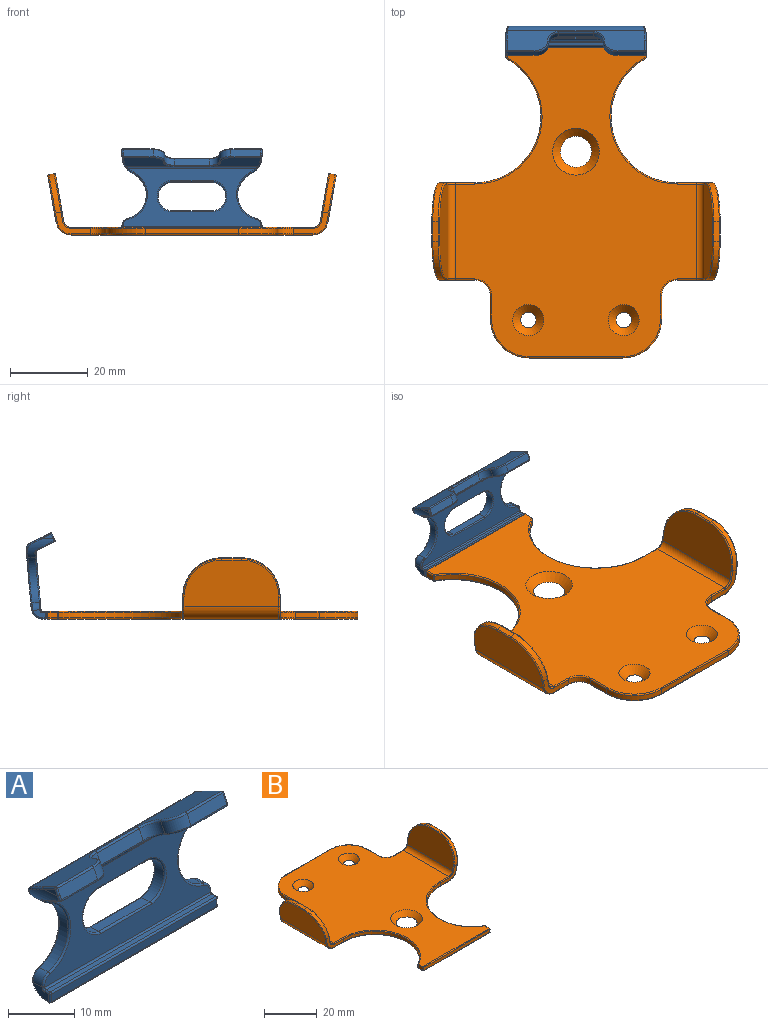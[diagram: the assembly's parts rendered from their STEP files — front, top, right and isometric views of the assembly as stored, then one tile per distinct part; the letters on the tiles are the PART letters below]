
ASSEMBLY  parts=2 mates=1
PART A: 107 faces, bbox 36.3x7.8x22.5 mm
  f0: plane 35.4x14.87mm, normal (0,-1,0.09), area 267.4mm2, adj f16,f17,f25,f26,f27,f28,f43,f44
  f1: plane 35.22x14.86mm, normal (0,1,-0.09), area 265.9mm2, adj f10,f15,f29,f30,f31,f32,f52,f53
  f2: plane 3.27x2.09mm, normal (1,0,0), area 4.5mm2, adj f35,f56,f57,f72,f73,f74,f102
  f3: plane 3.27x2.09mm, normal (-1,0,0), area 4.5mm2, adj f36,f46,f47,f48,f58,f59,f103
  f4: plane 11.89x4.49mm, normal (0,-0.45,-0.89), area 50.1mm2, adj f16,f41,f85,f87,f89
  f5: plane 35.4x5.1mm, normal (0,0.45,0.89), area 124.1mm2, adj f10,f49,f50,f65,f66,f86,f88,f90
  f6: plane 7.7x1.7mm, normal (0,-0.89,0.45), area 14.6mm2, adj f39,f76,f80,f82,f86
  f7: plane 35.4x0.82mm, normal (0,0,1), area 29.1mm2, adj f17,f48,f74,f106
  f8: plane 35.4x1.4mm, normal (0,-1,0), area 49.6mm2, adj f99,f102,f103,f106
  f9: plane 35.4x0.68mm, normal (0,0,-1), area 24.2mm2, adj f15,f57,f58,f99
  f10: cylinder r=2mm len=35.17mm, axis (-1,0,0), area 82.8mm2, adj f1,f5,f51,f64
  f11: plane 7.7x1.7mm, normal (0,-0.89,0.45), area 14.6mm2, adj f40,f89,f93,f95,f98
  f12: plane 11.89x4.49mm, normal (0,-0.45,-0.89), area 50.1mm2, adj f16,f67,f75,f76,f77
  f13: plane 3.08x1.29mm, normal (1,0,0), area 1.6mm2, adj f33,f49,f82
  f14: plane 3.08x1.29mm, normal (-1,0,0), area 1.6mm2, adj f34,f66,f95
  f15: cylinder r=3mm len=35.4mm, axis (-1,0,0), area 157.5mm2, adj f1,f9,f55,f56,f59,f60
  f16: cylinder r=0.5mm len=33.89mm, axis (1,0,0), area 17.9mm2, adj f0,f4,f12,f42,f68,f79,f81,f83
  f17: cylinder r=0.3mm len=35.4mm, axis (1,0,0), area 15.8mm2, adj f0,f7,f47,f73
  f18: plane 9x1.75mm, normal (0,-0.89,0.45), area 17.6mm2, adj f37,f38,f81,f92
  f19: cylinder r=6.25mm len=11.78mm, axis (0,1,-0.09), area 28.9mm2, adj f34,f36,f44,f62
  f20: cylinder r=6.25mm len=11.78mm, axis (0,1,-0.09), area 28.9mm2, adj f33,f35,f53,f70
  f21: plane 11x1.89mm, normal (0,0.09,1), area 20.9mm2, adj f22,f24,f26,f29
  f22: cylinder r=3.8mm len=7.64mm, axis (0,1,-0.09), area 20.3mm2, adj f21,f23,f25,f30
  f23: plane 11x1.89mm, normal (0,-0.09,-1), area 20.9mm2, adj f22,f24,f27,f32
  f24: cylinder r=3.8mm len=7.64mm, axis (0,1,-0.09), area 20.3mm2, adj f21,f23,f28,f31
  f25: torus R=4.1mm, axis (0,1,-0.09), area 5.2mm2, adj f0,f22,f26,f27
  f26: cylinder r=0.3mm len=11.05mm, axis (1,0,0), area 5.2mm2, adj f0,f21,f25,f28
  f27: cylinder r=0.3mm len=11.05mm, axis (-1,0,0), area 5.2mm2, adj f0,f23,f25,f28
  f28: torus R=4.1mm, axis (0,1,-0.09), area 5.2mm2, adj f0,f24,f26,f27
  f29: cylinder r=0.3mm len=11.05mm, axis (-1,0,0), area 5.2mm2, adj f1,f21,f30,f31
  f30: torus R=4.1mm, axis (0,-1,0.09), area 5.2mm2, adj f1,f22,f29,f32
  f31: torus R=4.1mm, axis (0,-1,0.09), area 5.2mm2, adj f1,f24,f29,f32
  f32: cylinder r=0.3mm len=11.05mm, axis (1,0,0), area 5.2mm2, adj f1,f23,f30,f31
  f33: cylinder r=5mm len=7.44mm, axis (0,1,-0.09), area 17.3mm2, adj f13,f20,f50,f51,f52,f67,f68,f69
  f34: cylinder r=5mm len=7.44mm, axis (0,1,-0.09), area 17.3mm2, adj f14,f19,f41,f42,f43,f63,f64,f65
  f35: cylinder r=2mm len=2.1mm, axis (0,1,-0.09), area 5mm2, adj f2,f20,f54,f55,f71
  f36: cylinder r=2mm len=2.1mm, axis (0,1,-0.09), area 5mm2, adj f3,f19,f45,f60,f61
  f37: cylinder r=2.5mm len=3.04mm, axis (0,-0.45,-0.89), area 7.3mm2, adj f18,f39,f77,f79,f90
  f38: cylinder r=2.5mm len=3.04mm, axis (0,0.45,0.89), area 7.3mm2, adj f18,f40,f83,f85,f94
  f39: cylinder r=3mm len=3.45mm, axis (0,-0.45,-0.89), area 8.8mm2, adj f6,f37,f75,f88
  f40: cylinder r=3mm len=3.45mm, axis (0,0.45,0.89), area 8.8mm2, adj f11,f38,f87,f96
  f41: bspline ~4.61x2.47mm, area 1.9mm2, adj f4,f34,f42,f91
  f42: bspline ~1.15x1.14mm, area 0.4mm2, adj f16,f34,f41,f43
  f43: torus R=4.7mm, axis (0,1,-0.09), area 0.8mm2, adj f0,f34,f42,f44
  f44: torus R=6.55mm, axis (0,1,-0.09), area 7.3mm2, adj f0,f19,f43,f45
  f45: torus R=1.7mm, axis (0,1,-0.09), area 1.2mm2, adj f0,f36,f44,f46
  f46: cylinder r=0.3mm len=0.31mm, axis (0,-0.09,-1), area 0.1mm2, adj f0,f3,f45,f47
  f47: torus R=0.6mm, axis (1,0,0), area 0.3mm2, adj f3,f17,f46,f48
  f48: cylinder r=0.3mm len=0.82mm, axis (0,-1,0), area 0.4mm2, adj f3,f7,f47,f105
  f49: cylinder r=0.3mm len=2.71mm, axis (0,0.89,-0.45), area 1.4mm2, adj f5,f13,f50,f84
  f50: bspline ~4.11x2.33mm, area 1.4mm2, adj f5,f33,f49,f51
  f51: bspline ~2.43x1.6mm, area 1.3mm2, adj f10,f33,f50,f52
  f52: torus R=4.7mm, axis (0,-1,0.09), area 1.2mm2, adj f1,f33,f51,f53
  f53: torus R=6.55mm, axis (0,-1,0.09), area 7.3mm2, adj f1,f20,f52,f54
  f54: torus R=1.7mm, axis (0,-1,0.09), area 0.9mm2, adj f1,f35,f53,f55
  f55: bspline ~1.55x0.55mm, area 0.3mm2, adj f15,f35,f54,f56
  f56: torus R=2.7mm, axis (1,0,0), area 1.7mm2, adj f2,f15,f55,f57
  f57: cylinder r=0.3mm len=0.68mm, axis (0,-1,0), area 0.3mm2, adj f2,f9,f56,f100
  f58: cylinder r=0.3mm len=0.68mm, axis (0,1,0), area 0.3mm2, adj f3,f9,f59,f101
  f59: torus R=2.7mm, axis (1,0,0), area 1.7mm2, adj f3,f15,f58,f60
  f60: bspline ~1.26x0.55mm, area 0.3mm2, adj f15,f36,f59,f61
  f61: torus R=1.7mm, axis (0,-1,0.09), area 0.9mm2, adj f1,f36,f60,f62
  f62: torus R=6.55mm, axis (0,-1,0.09), area 7.3mm2, adj f1,f19,f61,f63
  f63: torus R=4.7mm, axis (0,-1,0.09), area 1.2mm2, adj f1,f34,f62,f64
  f64: bspline ~2.7x1.4mm, area 1.3mm2, adj f10,f34,f63,f65
  f65: bspline ~4.11x2.33mm, area 1.4mm2, adj f5,f34,f64,f66
  f66: cylinder r=0.3mm len=2.71mm, axis (0,-0.89,0.45), area 1.4mm2, adj f5,f14,f65,f97
  f67: bspline ~4.61x2.47mm, area 1.9mm2, adj f12,f33,f68,f78
  f68: bspline ~1.15x1.14mm, area 0.4mm2, adj f16,f33,f67,f69
  f69: torus R=4.7mm, axis (0,1,-0.09), area 0.8mm2, adj f0,f33,f68,f70
  f70: torus R=6.55mm, axis (0,1,-0.09), area 7.3mm2, adj f0,f20,f69,f71
  f71: torus R=1.7mm, axis (0,1,-0.09), area 1.2mm2, adj f0,f35,f70,f72
  f72: cylinder r=0.3mm len=0.31mm, axis (0,0.09,1), area 0.1mm2, adj f0,f2,f71,f73
  f73: torus R=0.6mm, axis (1,0,0), area 0.3mm2, adj f2,f17,f72,f74
  f74: cylinder r=0.3mm len=0.82mm, axis (0,1,0), area 0.4mm2, adj f2,f7,f73,f104
  f75: torus R=2.7mm, axis (0,0.45,0.89), area 2.1mm2, adj f12,f39,f76,f77
  f76: cylinder r=0.3mm len=7.65mm, axis (-1,0,0), area 3.6mm2, adj f6,f12,f75,f78
  f77: torus R=2.8mm, axis (0,0.45,0.89), area 1.3mm2, adj f12,f37,f75,f79
  f78: sphere r=0.3mm, area 0.1mm2, adj f67,f76,f80
  f79: bspline ~1.76x0.52mm, area 0.5mm2, adj f16,f37,f77,f81
  f80: bspline ~1.79x1.09mm, area 0.4mm2, adj f6,f33,f78,f82
  f81: cylinder r=0.3mm len=9mm, axis (1,0,0), area 3.2mm2, adj f16,f18,f79,f83
  f82: cylinder r=0.3mm len=1.15mm, axis (0,0.45,0.89), area 0.5mm2, adj f6,f13,f80,f84
  f83: bspline ~2.03x0.55mm, area 0.5mm2, adj f16,f38,f81,f85
  f84: sphere r=0.3mm, area 0.1mm2, adj f49,f82,f86
  f85: torus R=2.8mm, axis (0,0.45,0.89), area 1.3mm2, adj f4,f38,f83,f87
  f86: cylinder r=0.3mm len=7.7mm, axis (-1,0,0), area 3.6mm2, adj f5,f6,f84,f88
  f87: torus R=2.7mm, axis (0,0.45,0.89), area 2.1mm2, adj f4,f40,f85,f89
  f88: torus R=2.7mm, axis (0,-0.45,-0.89), area 2.1mm2, adj f5,f39,f86,f90
  f89: cylinder r=0.3mm len=7.65mm, axis (-1,0,0), area 3.6mm2, adj f4,f11,f87,f91
  f90: torus R=2.8mm, axis (0,-0.45,-0.89), area 1.9mm2, adj f5,f37,f88,f92
  f91: sphere r=0.3mm, area 0.1mm2, adj f41,f89,f93
  f92: cylinder r=0.3mm len=9mm, axis (-1,0,0), area 4.2mm2, adj f5,f18,f90,f94
  f93: bspline ~1.79x1.09mm, area 0.4mm2, adj f11,f34,f91,f95
  f94: torus R=2.8mm, axis (0,-0.45,-0.89), area 1.9mm2, adj f5,f38,f92,f96
  f95: cylinder r=0.3mm len=1.15mm, axis (0,-0.45,-0.89), area 0.5mm2, adj f11,f14,f93,f97
  f96: torus R=2.7mm, axis (0,-0.45,-0.89), area 2.1mm2, adj f5,f40,f94,f98
  f97: sphere r=0.3mm, area 0.1mm2, adj f66,f95,f98
  f98: cylinder r=0.3mm len=7.7mm, axis (-1,0,0), area 3.6mm2, adj f5,f11,f96,f97
  f99: cylinder r=0.3mm len=35.4mm, axis (-1,0,0), area 16.7mm2, adj f8,f9,f100,f101
  f100: sphere r=0.3mm, area 0.1mm2, adj f57,f99,f102
  f101: sphere r=0.3mm, area 0.1mm2, adj f58,f99,f103
  f102: cylinder r=0.3mm len=1.4mm, axis (0,0,1), area 0.7mm2, adj f2,f8,f100,f104
  f103: cylinder r=0.3mm len=1.4mm, axis (0,0,-1), area 0.7mm2, adj f3,f8,f101,f105
  f104: sphere r=0.3mm, area 0.1mm2, adj f74,f102,f106
  f105: sphere r=0.3mm, area 0.1mm2, adj f48,f103,f106
  f106: cylinder r=0.3mm len=35.4mm, axis (-1,0,0), area 16.7mm2, adj f7,f8,f104,f105
PART B: 104 faces, bbox 74.3x80.8x16.9 mm
  f0: plane 35.4x1.4mm, normal (0,-1,0), area 49.6mm2, adj f84,f88,f92,f93
  f1: plane 2.52x1.4mm, normal (1,0,0), area 3.5mm2, adj f75,f79,f84,f85
  f2: cylinder r=17mm len=31.92mm, axis (0,0,-1), area 62.9mm2, adj f3,f70,f75,f76
  f3: plane 9.05x5.62mm, normal (0,-1,0), area 16.2mm2, adj f2,f29,f58,f62,f63,f66,f67,f71
  f4: plane 9.05x5.62mm, normal (0,1,0), area 16.2mm2, adj f5,f31,f37,f39,f40,f42,f43,f47
  f5: cylinder r=4mm len=4mm, axis (0,0,-1), area 8.8mm2, adj f4,f6,f35,f44
  f6: plane 6x1.4mm, normal (1,0,0), area 8.4mm2, adj f5,f7,f36,f48
  f7: cylinder r=10mm len=10mm, axis (0,0,-1), area 22mm2, adj f6,f8,f38,f52
  f8: plane 24x1.4mm, normal (0,1,0), area 33.6mm2, adj f7,f9,f41,f56
  f9: cylinder r=10mm len=10mm, axis (0,0,-1), area 22mm2, adj f8,f10,f45,f60
  f10: plane 6x1.4mm, normal (-1,0,0), area 8.4mm2, adj f9,f11,f49,f64
  f11: cylinder r=4mm len=4mm, axis (0,0,-1), area 8.8mm2, adj f10,f12,f53,f68
  f12: plane 9.05x5.62mm, normal (0,1,0), area 16.2mm2, adj f11,f24,f57,f61,f65,f72,f77,f81
  f13: plane 9.05x5.62mm, normal (0,-1,0), area 16.2mm2, adj f14,f22,f82,f87,f91,f97,f100,f102
  f14: cylinder r=17mm len=31.92mm, axis (0,0,-1), area 62.9mm2, adj f13,f95,f98,f103
  f15: plane 2.52x1.7mm, normal (-1,0,0), area 4.3mm2, adj f16,f92,f95,f98,f99
  f16: plane 79.4x62mm, normal (0,0,1), area 2997.1mm2, adj f15,f18,f25,f32,f33,f34,f35,f36
  f17: plane 79.4x62mm, normal (0,0,-1), area 3134.6mm2, adj f21,f28,f32,f33,f34,f40,f44,f48
  f18: cylinder r=2mm len=24.4mm, axis (0,-1,0), area 68.1mm2, adj f16,f19,f61,f87
  f19: plane 24.4x11.87mm, normal (0.98,0,0.17), area 253.7mm2, adj f18,f65,f69,f73,f78,f82
  f20: plane 24.4x11.87mm, normal (-0.98,0,-0.17), area 253.7mm2, adj f21,f81,f86,f90,f94,f97
  f21: cylinder r=4mm len=24.4mm, axis (0,-1,0), area 136.3mm2, adj f17,f20,f77,f100
  f22: cylinder r=10mm len=10.09mm, axis (-0.98,0,-0.17), area 22mm2, adj f13,f23,f78,f94
  f23: plane 5x1.38mm, normal (-0.17,0,0.98), area 7mm2, adj f22,f24,f73,f90
  f24: cylinder r=10mm len=10.09mm, axis (-0.98,0,-0.17), area 22mm2, adj f12,f23,f69,f86
  f25: cylinder r=2mm len=24.4mm, axis (0,-1,0), area 68.1mm2, adj f16,f26,f39,f62
  f26: plane 24.4x11.87mm, normal (-0.98,0,0.17), area 253.7mm2, adj f25,f42,f46,f50,f54,f58
  f27: plane 24.4x11.87mm, normal (0.98,0,-0.17), area 253.7mm2, adj f28,f47,f51,f55,f59,f63
  f28: cylinder r=4mm len=24.4mm, axis (0,-1,0), area 136.3mm2, adj f17,f27,f43,f67
  f29: cylinder r=10mm len=10.09mm, axis (0.98,0,-0.17), area 22mm2, adj f3,f30,f54,f59
  f30: plane 5x1.38mm, normal (0.17,0,0.98), area 7mm2, adj f29,f31,f50,f55
  f31: cylinder r=10mm len=10.09mm, axis (0.98,0,-0.17), area 22mm2, adj f4,f30,f46,f51
  f32: cone r=2mm half-angle=45deg, axis (0,0,1), area 53.3mm2, adj f16,f17
  f33: cone r=2mm half-angle=45deg, axis (0,0,1), area 53.3mm2, adj f16,f17
  f34: cone r=4mm half-angle=45deg, axis (0,0,1), area 88.9mm2, adj f16,f17
  f35: torus R=4.3mm, axis (0,0,1), area 3mm2, adj f5,f16,f36,f37
  f36: cylinder r=0.3mm len=6mm, axis (0,-1,0), area 2.8mm2, adj f6,f16,f35,f38
  f37: cylinder r=0.3mm len=5mm, axis (1,0,0), area 2.4mm2, adj f4,f16,f35,f39
  f38: torus R=9.7mm, axis (0,0,1), area 7.3mm2, adj f7,f16,f36,f41
  f39: torus R=2.3mm, axis (0,1,0), area 1.4mm2, adj f4,f25,f37,f42
  f40: cylinder r=0.3mm len=5mm, axis (-1,0,0), area 2.4mm2, adj f4,f17,f43,f44
  f41: cylinder r=0.3mm len=24mm, axis (1,0,0), area 11.3mm2, adj f8,f16,f38,f45
  f42: cylinder r=0.3mm len=2.37mm, axis (-0.17,0,-0.98), area 1.1mm2, adj f4,f26,f39,f46
  f43: torus R=3.7mm, axis (0,1,0), area 2.6mm2, adj f4,f28,f40,f47
  f44: torus R=4.3mm, axis (0,0,1), area 3mm2, adj f5,f17,f40,f48
  f45: torus R=9.7mm, axis (0,0,1), area 7.3mm2, adj f9,f16,f41,f49
  f46: torus R=9.7mm, axis (0.98,0,-0.17), area 7.3mm2, adj f26,f31,f42,f50
  f47: cylinder r=0.3mm len=2.37mm, axis (0.17,0,0.98), area 1.1mm2, adj f4,f27,f43,f51
  f48: cylinder r=0.3mm len=6mm, axis (0,1,0), area 2.8mm2, adj f6,f17,f44,f52
  f49: cylinder r=0.3mm len=6mm, axis (0,1,0), area 2.8mm2, adj f10,f16,f45,f53
  f50: cylinder r=0.3mm len=5mm, axis (0,1,0), area 2.4mm2, adj f26,f30,f46,f54
  f51: torus R=9.7mm, axis (-0.98,0,0.17), area 7.3mm2, adj f27,f31,f47,f55
  f52: torus R=9.7mm, axis (0,0,1), area 7.3mm2, adj f7,f17,f48,f56
  f53: torus R=4.3mm, axis (0,0,1), area 3mm2, adj f11,f16,f49,f57
  f54: torus R=9.7mm, axis (0.98,0,-0.17), area 7.3mm2, adj f26,f29,f50,f58
  f55: cylinder r=0.3mm len=5mm, axis (0,-1,0), area 2.4mm2, adj f27,f30,f51,f59
  f56: cylinder r=0.3mm len=24mm, axis (-1,0,0), area 11.3mm2, adj f8,f17,f52,f60
  f57: cylinder r=0.3mm len=5mm, axis (1,0,0), area 2.4mm2, adj f12,f16,f53,f61
  f58: cylinder r=0.3mm len=2.37mm, axis (0.17,0,0.98), area 1.1mm2, adj f3,f26,f54,f62
  f59: torus R=9.7mm, axis (-0.98,0,0.17), area 7.3mm2, adj f27,f29,f55,f63
  f60: torus R=9.7mm, axis (0,0,1), area 7.3mm2, adj f9,f17,f56,f64
  f61: torus R=2.3mm, axis (0,-1,0), area 1.4mm2, adj f12,f18,f57,f65
  f62: torus R=2.3mm, axis (0,-1,0), area 1.4mm2, adj f3,f25,f58,f66
  f63: cylinder r=0.3mm len=2.37mm, axis (-0.17,0,-0.98), area 1.1mm2, adj f3,f27,f59,f67
  f64: cylinder r=0.3mm len=6mm, axis (0,-1,0), area 2.8mm2, adj f10,f17,f60,f68
  f65: cylinder r=0.3mm len=2.37mm, axis (-0.17,0,0.98), area 1.1mm2, adj f12,f19,f61,f69
  f66: cylinder r=0.3mm len=5mm, axis (-1,0,0), area 2.4mm2, adj f3,f16,f62,f70
  f67: torus R=3.7mm, axis (0,-1,0), area 2.6mm2, adj f3,f28,f63,f71
  f68: torus R=4.3mm, axis (0,0,1), area 3mm2, adj f11,f17,f64,f72
  f69: torus R=9.7mm, axis (-0.98,0,-0.17), area 7.3mm2, adj f19,f24,f65,f73
  f70: torus R=17.3mm, axis (0,0,1), area 21.3mm2, adj f2,f16,f66,f74
  f71: cylinder r=0.3mm len=5mm, axis (1,0,0), area 2.4mm2, adj f3,f17,f67,f76
  f72: cylinder r=0.3mm len=5mm, axis (-1,0,0), area 2.4mm2, adj f12,f17,f68,f77
  f73: cylinder r=0.3mm len=5mm, axis (0,1,0), area 2.4mm2, adj f19,f23,f69,f78
  f74: sphere r=0.3mm, area 0.1mm2, adj f70,f75,f79
  f75: cylinder r=0.3mm len=1.4mm, axis (0,0,-1), area 0.4mm2, adj f1,f2,f74,f80
  f76: torus R=17.3mm, axis (0,0,1), area 21.3mm2, adj f2,f17,f71,f80
  f77: torus R=3.7mm, axis (0,-1,0), area 2.6mm2, adj f12,f21,f72,f81
  f78: torus R=9.7mm, axis (-0.98,0,-0.17), area 7.3mm2, adj f19,f22,f73,f82
  f79: cylinder r=0.3mm len=2.52mm, axis (0,-1,0), area 1.2mm2, adj f1,f16,f74,f83
  f80: sphere r=0.3mm, area 0.1mm2, adj f75,f76,f85
  f81: cylinder r=0.3mm len=2.37mm, axis (0.17,0,-0.98), area 1.1mm2, adj f12,f20,f77,f86
  f82: cylinder r=0.3mm len=2.37mm, axis (0.17,0,-0.98), area 1.1mm2, adj f13,f19,f78,f87
  f83: sphere r=0.3mm, area 0.1mm2, adj f79,f84,f88
  f84: cylinder r=0.3mm len=1.4mm, axis (0,0,-1), area 0.7mm2, adj f0,f1,f83,f89
  f85: cylinder r=0.3mm len=2.52mm, axis (0,1,0), area 1.2mm2, adj f1,f17,f80,f89
  f86: torus R=9.7mm, axis (0.98,0,0.17), area 7.3mm2, adj f20,f24,f81,f90
  f87: torus R=2.3mm, axis (0,1,0), area 1.4mm2, adj f13,f18,f82,f91
  f88: cylinder r=0.3mm len=35.7mm, axis (-1,0,0), area 16.8mm2, adj f0,f16,f83,f92
  f89: sphere r=0.3mm, area 0.1mm2, adj f84,f85,f93
  f90: cylinder r=0.3mm len=5mm, axis (0,-1,0), area 2.4mm2, adj f20,f23,f86,f94
  f91: cylinder r=0.3mm len=5mm, axis (-1,0,0), area 2.4mm2, adj f13,f16,f87,f95
  f92: cylinder r=0.3mm len=1.7mm, axis (0,0,1), area 0.7mm2, adj f0,f15,f88,f96
  f93: cylinder r=0.3mm len=35.4mm, axis (1,0,0), area 16.7mm2, adj f0,f17,f89,f96
  f94: torus R=9.7mm, axis (0.98,0,0.17), area 7.3mm2, adj f20,f22,f90,f97
  f95: torus R=17.3mm, axis (0,0,1), area 21.4mm2, adj f14,f15,f16,f91,f98
  f96: sphere r=0.3mm, area 0.1mm2, adj f92,f93,f99
  f97: cylinder r=0.3mm len=2.37mm, axis (-0.17,0,0.98), area 1.1mm2, adj f13,f20,f94,f100
  f98: cylinder r=0.3mm len=1.66mm, axis (0,0,-1), area 0.5mm2, adj f14,f15,f95,f101
  f99: cylinder r=0.3mm len=2.52mm, axis (0,-1,0), area 1.2mm2, adj f15,f17,f96,f101
  f100: torus R=3.7mm, axis (0,1,0), area 2.6mm2, adj f13,f21,f97,f102
  f101: sphere r=0.3mm, area 0.1mm2, adj f98,f99,f103
  f102: cylinder r=0.3mm len=5mm, axis (1,0,0), area 2.4mm2, adj f13,f17,f100,f103
  f103: torus R=17.3mm, axis (0,0,1), area 21.3mm2, adj f14,f17,f101,f102
PLACE A t=(0.84,-19.28,-9.23)mm
PLACE B rot(axis=(0,0,-1),180deg) t=(0.84,-61.28,-9.23)mm
MATE fastened B.f0 <-> A.f8  axis (0,1,0) through (0.84,-19.28,-8.23)mm
